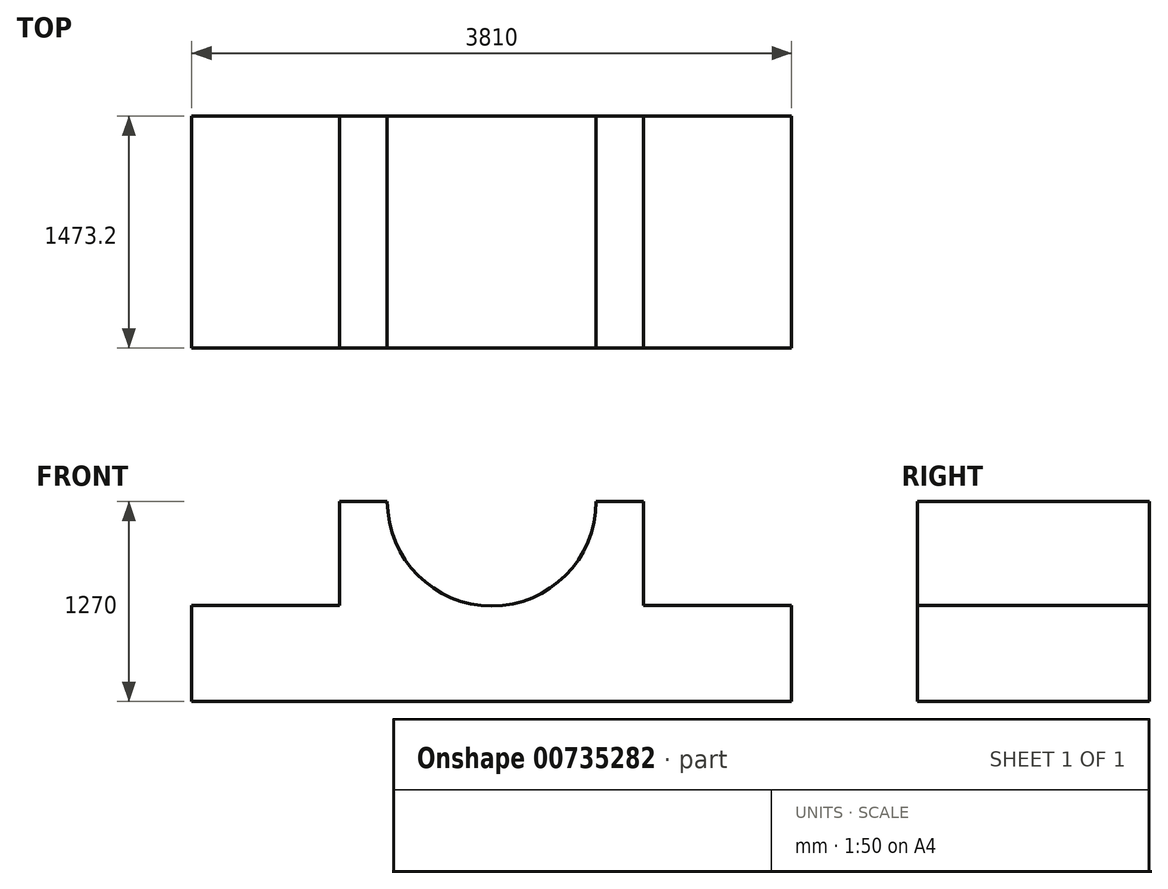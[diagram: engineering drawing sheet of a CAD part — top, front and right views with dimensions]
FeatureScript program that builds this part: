
annotation { "Feature Type Name" : "Feature", "Feature Type Description" : "" }
export const myFeature = defineFeature(function(context is Context, id is Id, definition is map)
    precondition{}
    {
        {
            var Q0;
            Q0=qCreatedBy(makeId("Front.planeOp"),FACE);
            var sketch = newSketch(context, id + "F0", { "sketchPlane" : qUnion([Q0])});
            skLineSegment(sketch, "E0", {"start": v(-143.92, 5.26) * mm, "end": v(3666.08, 5.26) * mm});
            skLineSegment(sketch, "E1", {"start": v(3666.08, 5.26) * mm, "end": v(3666.08, 614.86) * mm});
            skLineSegment(sketch, "E2", {"start": v(-143.92, 5.26) * mm, "end": v(-143.92, 614.86) * mm});
            skLineSegment(sketch, "E3", {"start": v(-143.92, 614.86) * mm, "end": v(795.88, 614.86) * mm});
            skLineSegment(sketch, "E4", {"start": v(3666.08, 614.86) * mm, "end": v(2726.28, 614.86) * mm});
            skLineSegment(sketch, "E5", {"start": v(795.88, 614.86) * mm, "end": v(795.88, 1275.26) * mm});
            skLineSegment(sketch, "E6", {"start": v(2726.28, 614.86) * mm, "end": v(2726.28, 1275.26) * mm});
            skLineSegment(sketch, "E7", {"start": v(795.88, 1275.26) * mm, "end": v(1100.68, 1275.26) * mm});
            skLineSegment(sketch, "E8", {"start": v(2726.28, 1275.26) * mm, "end": v(2421.48, 1275.26) * mm});
            skLineSegment(sketch, "E9", {"start": v(1100.68, 1275.26) * mm, "end": v(1761.08, 1275.26) * mm});
            skCircle(sketch, "E10", {"center": v(1761.08, 1275.26) * mm, "radius": 663.5 * mm});
            skSolve(sketch);
        }
        {
            var Q0;
            Q0=makeQuery(id+"F0.imprint","IMPRINT",FACE,{"disambiguationData":[TD([[makeQuery(id+"F0.imprint","IMPRINT",EDGE,{"derivedFrom":sQuery(id+"F0.wireOp",EDGE,"E0")}),1.0]])]});
            extrude(context, id + "F1", {"entities" : qUnion([Q0]), "depth" : 1473.2 * mm, "offsetDistance" : 25.4 * mm});
        }
    });
